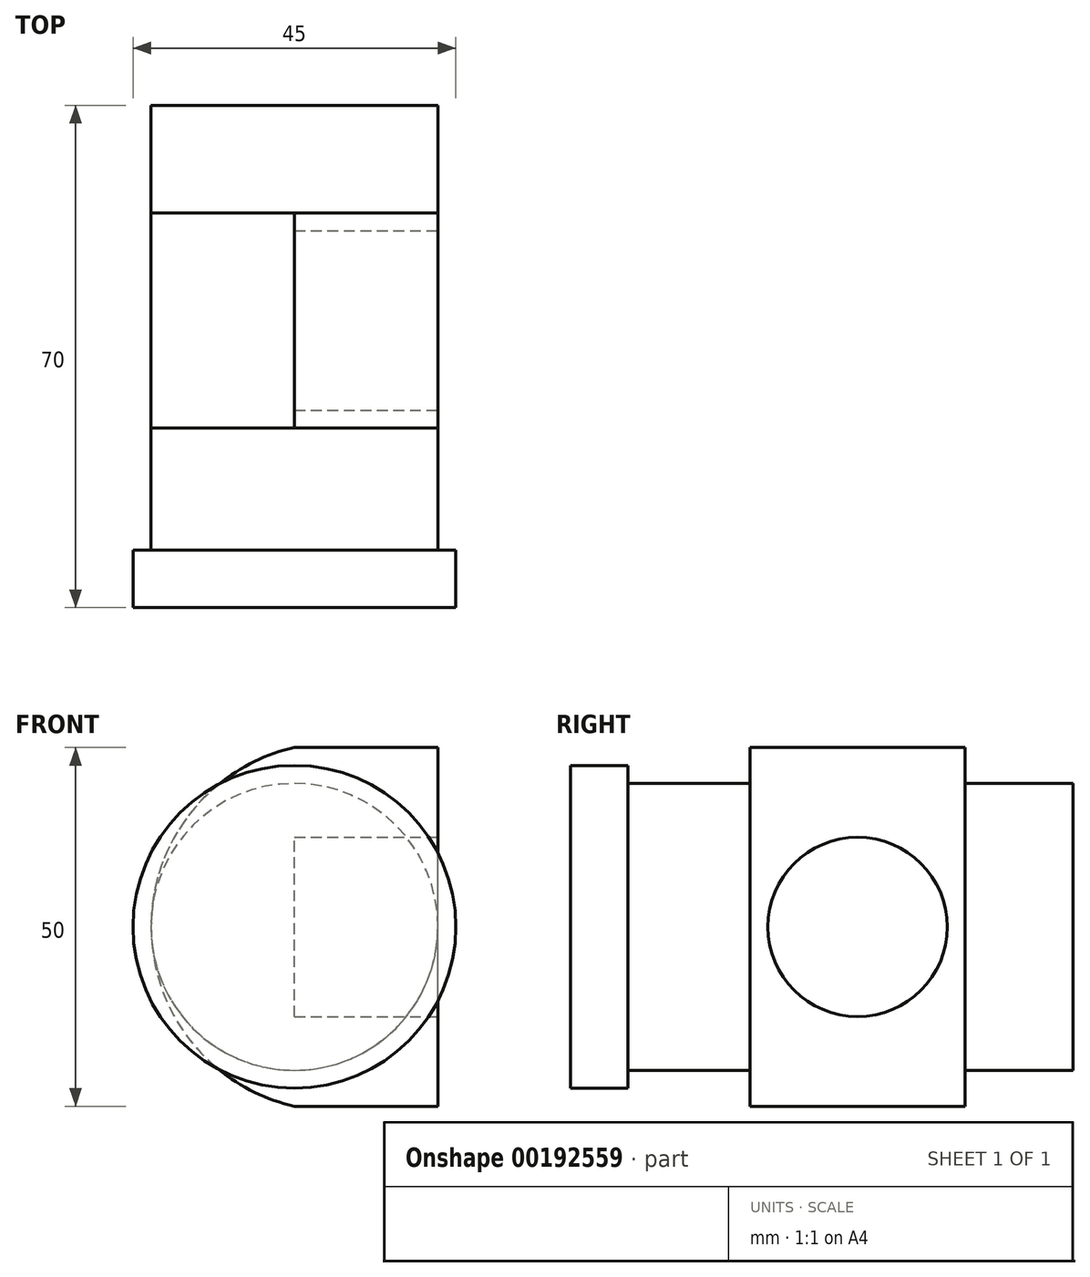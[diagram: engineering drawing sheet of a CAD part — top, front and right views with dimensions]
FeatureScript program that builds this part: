
annotation { "Feature Type Name" : "Feature", "Feature Type Description" : "" }
export const myFeature = defineFeature(function(context is Context, id is Id, definition is map)
    precondition{}
    {
        {
            var Q0;
            Q0=qCreatedBy(makeId("Front.planeOp"),FACE);
            var sketch = newSketch(context, id + "F0", { "sketchPlane" : qUnion([Q0])});
            skCircle(sketch, "E0", {"center": v(0, 0) * mm, "radius": 20 * mm});
            skSolve(sketch);
        }
        {
            var Q0;
            Q0=qSketchRegion(id+"F0",true);
            extrude(context, id + "F1", {"entities" : qUnion([Q0]), "depth" : 70 * mm});
        }
        {
            var Q0;
            Q0=qCreatedBy(makeId("Front.planeOp"),FACE);
            cPlane(context, id + "F2", {"entities" : qUnion([Q0]), "cplaneType" : CPlaneType.OFFSET, "offset" : 15 * mm, "width" : 150 * mm, "height" : 150 * mm});
        }
        {
            var Q0;
            Q0=qCreatedBy(id+"F2.planeOp",FACE);
            var sketch = newSketch(context, id + "F3", { "sketchPlane" : qUnion([Q0])});
            skLineSegment(sketch, "E1.bottom", {"start": v(-20, -25) * mm, "end": v(20, -25) * mm});
            skLineSegment(sketch, "E1.top", {"start": v(-20, 25) * mm, "end": v(20, 25) * mm});
            skLineSegment(sketch, "E1.left", {"start": v(-20, -25) * mm, "end": v(-20, 25) * mm});
            skLineSegment(sketch, "E1.right", {"start": v(20, -25) * mm, "end": v(20, 25) * mm});
            skPoint(sketch, "E1.middle", {"position": v(0, 0) * mm});
            skSolve(sketch);
        }
        {
            var Q0;
            Q0=qSketchRegion(id+"F3",true);
            extrude(context, id + "F4", {"entities" : qUnion([Q0]), "operationType" : NewBodyOperationType.ADD, "depth" : 30 * mm});
        }
        {
            var Q0;
            Q0=makeQuery(id+"F4.opExtrude","SWEPT_FACE",FACE,{"disambiguationData":[OSD([sQuery(id+"F3.wireOp",EDGE,"E1.right")])]});
            var sketch = newSketch(context, id + "F5", { "sketchPlane" : qUnion([Q0])});
            skCircle(sketch, "E2", {"center": v(-30, 0) * mm, "radius": 12.5 * mm});
            skSolve(sketch);
        }
        {
            var Q0;
            Q0=qSketchRegion(id+"F5",true);
            extrude(context, id + "F6", {"entities" : qUnion([Q0]), "operationType" : NewBodyOperationType.REMOVE, "oppositeDirection" : true, "depth" : 20 * mm});
        }
        {
            var Q0;
            {var subQ0=sQuery(id+"F3.wireOp",EDGE,"E1.left");var subQ1=sQuery(id+"F3.wireOp",EDGE,"E1.top");var subQ2=sQuery(id+"F3.wireOp",EDGE,"E1.right");var subQ3=makeQuery(id+"F4.opExtrude","CAP_FACE",FACE,{"disambiguationData":[OSD([sQuery(id+"F3.wireOp",EDGE,"E1.bottom"),subQ1,subQ0,subQ2])],"isStart":false});Q0=makeQuery(id+"F4.boolean.opBoolean","SPLIT",FACE,{"disambiguationData":[TD([makeQuery(id+"F4.opExtrude","SWEPT_FACE",FACE,{"disambiguationData":[OSD([subQ1])]})])],"derivedFrom":subQ3});}
            var sketch = newSketch(context, id + "F7", { "sketchPlane" : qUnion([Q0])});
            skArc(sketch, "E3", {"start": v(0, 25) * mm, "mid": v(-20, 0) * mm, "end": v(0, -25) * mm});
            skPoint(sketch, "E3.endSnap0", {"position": v(0, 20) * mm});
            skLineSegment(sketch, "E4", {"start": v(0, 25) * mm, "end": v(-20, 25) * mm});
            skLineSegment(sketch, "E5", {"start": v(-20, 25) * mm, "end": v(-20, -25) * mm});
            skLineSegment(sketch, "E6", {"start": v(-20, -25) * mm, "end": v(0, -25) * mm});
            skSolve(sketch);
        }
        {
            var Q0;
            Q0 = qSketchRegion(id + "F7", true);
            extrude(context, id + "F8", {"entities" : qUnion([Q0]), "operationType" : NewBodyOperationType.REMOVE, "endBound" : BoundingType.UP_TO_NEXT, "oppositeDirection" : true, "depth" : 25 * mm});
        }
        {
            var Q0;
            Q0=makeQuery(id+"F1.opExtrude","CAP_FACE",FACE,{"disambiguationData":[OSD([sQuery(id+"F0.wireOp",EDGE,"E0")])],"isStart":false});
            var sketch = newSketch(context, id + "F9", { "sketchPlane" : qUnion([Q0])});
            skCircle(sketch, "E7", {"center": v(0, 0) * mm, "radius": 22.5 * mm});
            skSolve(sketch);
        }
        {
            var Q0;
            Q0 = qSketchRegion(id + "F9", true);
            extrude(context, id + "F10", {"entities" : qUnion([Q0]), "operationType" : NewBodyOperationType.ADD, "oppositeDirection" : true, "depth" : 8 * mm});
        }
    });
